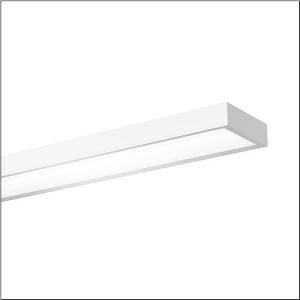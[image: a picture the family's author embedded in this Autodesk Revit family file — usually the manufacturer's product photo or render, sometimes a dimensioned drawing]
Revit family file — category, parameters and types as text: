
# Revit family: sport_31_51hs12dc4eca
name_source: partatom
category: Lighting Fixtures
units: mm (PartAtom-declared; Revit-internal decimal feet)

## family parameters
Cut with Voids When Loaded = No
Host = Face
Light Source = No
Part Type = Normal
Room Calculation Point = No
Round Connector Dimension = Use Diameter
Shared = No

## types (1)
- --- (1 x LED, 11990 lm, 89.4 W, 4000K)
    Apparent Load = 89 VA
    CIE Flux Codes = 65 89 97 100 100
    Color Rendering = 80
    Color Temperature = 4000K
    Default Elevation = 1800 mm
    Description = Sport 31, high bay luminaire, primary light control with reflector, of sheet steel, primary anti-glare with prismatic structure, of PC, primary optical cover: cover panel, of PC, light emission: direct distribution, primary light characteristic: symmetric, installation type: suspended mounting, recessed, surface-mounted, LED, rated luminous flux: 12.000lm, luminous efficacy: 137lm/W, light colour: 840, colour temperature: 4000K, control gear: DALI 2, with terminal, 5-pole, max. 2.5mm², mains connection: 220..240V, AC/DC, 50/60Hz, rated input power: 88W, housing, of sheet steel, traffic white (RAL 9016), length: 1.540mm, width: 315mm, height: 95mm, protection rating (complete): IP20, protection rating (lamp compartment, on room side): IP50, insulation class (complete): insulation class I (protective earthing), certification: CE, ENEC, UKCA, ball protection: ball impact resistant with ceiling mounting or chain suspension, impact resistance: IK08, permissible operating ambient temperature: -20..+35°C, standard: DIN 18032-3, EN 60598-2-22, packaging unit: 1 piece
    Height = 100 mm  [stored 0.328084 ft]
    Lamp = 1 x LED
    Lamp Light Flux = 11990 lm
    Lamp Power = 89.4 W
    Lamp count = 1
    Length = 1500 mm
    Luminous efficacy = 134 lm/W
    Manufacturer = Siteco
    ModVariant = No
    Model = 51HS12DC4ECA
    Mounting Place = Ceiling
    Mounting Type = Pendant
    Number of Poles = 1
    OnlyDefault = Yes
    Power Factor = 1
    Product Name = Sport 31
    Product group = high bay luminaire
    ProductGroupID = 902
    Protection Class = Protection class I
    Protection Degree = IP 20
    RLX_Detail_Level = 1
    RLX_Emergency_Light_Flux = 0 lm
    RLX_Emergency_Type = 0
    RLX_Emergency_Type_DB = No
    RlxData = <blob elided: 22813 chars, md5=9ac5c6be>
    Socket = socket
    Standby Power = 0 W
    System Light Flux = 11990 lm
    System Power = 89 W
    Type Comments = factory setting: luminous flux: 100 % | dim-lin: 254 | 380 mA
    Type Image = l_1397489.jpg
    URL = http://relux.com
    VarID = @adj_196209
    Voltage = 0 V
    Weight = 0.00 kg
    Width = 315 mm

note: [stored X ft] marks values corroborated as IEEE doubles in the binary element streams (Revit-internal decimal feet)

## geometry (parser evidence)
native form markers: Blend x4, Sweep x11
no freeform markers — native parametric forms only
